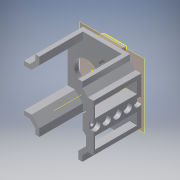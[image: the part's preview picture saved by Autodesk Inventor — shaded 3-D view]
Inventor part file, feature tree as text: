
AUTODESK INVENTOR PART (.ipt)
format: ipt  version: 2019 (Build 230136000, 136)  size: 473,088 bytes
history: native  units: mm
features: reference x25, other x11, sketch x10, extrude x9, projected_geometry x6, plane x5, chamfer x2, hole x2, pattern_circular x1, pattern_linear x1, fillet x1
ambient origin geometry x8: Origin, YZ Plane, XZ Plane, XY Plane, X Axis, Y Axis, Z Axis, Center Point
bodies: Solid1 (feature_tree)
feature tree (73):
  plane  "Work Plane1"
  extrude  "Extrusion1"  Depth=0.1mm
  chamfer  "Chamfer1"  Distance=3.0mm
  sketch  "Sketch2"  dims[d3=0.1mm]
  plane  "Work Plane2"
  extrude  "Extrusion2"  Depth=3.001102mm
  other  "Work Axis1"
  pattern_circular  "Circular Pattern1"  Count=4 Angle=360.0deg
  extrude  "Extrusion3"  Depth=1.0mm TaperAngle=0.0deg
  sketch  "Sketch4"  dims[d5=0.1mm]
  plane  "Work Plane3"
  extrude  "Extrusion4"  Depth=49.7mm
  extrude  "Extrusion5"  Depth=49.7mm
  pattern_linear  "Rectangular Pattern1"  Spacing1=2.8mm  [1 undecoded]
  sketch  "Sketch7"  dims[d6=3.0mm]
  plane  "Work Plane4"
  extrude  "Extrusion7"  Depth=10.0mm TaperAngle=0.0deg
  hole  "Hole1"  [1 undecoded]
  extrude  "Extrusion8"  Depth=19.0mm
  extrude  "Extrusion9"  TaperAngle=0.0deg  [1 undecoded]
  hole  "Hole2"  [1 undecoded]
  chamfer  "Chamfer2"  Distance=2.0mm
  fillet  "Fillet1"  Radius=3.0mm
  sketch  "Sketch14"  dims[d19=6.0mm d20=1.0mm d21=0.0mm]
  sketch  "Sketch15"  dims[d22=3.0mm d23=0.0mm d24=2.0mm d25=2.8mm d26=2.8mm d27=10.0mm d28=0.0mm d29=40.0mm d31=7.5mm d35=19.0mm d36=0.0mm d37=12.0mm d38=0.0mm d39=2.5mm d40=6.0mm d41=6.0mm d42=22.0mm d43=90.0deg d44=8.0mm d45=20.594885mm d46=2.0mm d47=3.0mm d48=0.0mm d50=3.0mm d51=0.0mm d56=2.8mm d57=6.0mm d58=6.0mm d59=3.0mm d60=90.0deg d61=8.0mm d62=20.594885mm d68=2.0mm d69=2.0mm d70=45.0deg d71=3.0mm d72=0.0mm d73=4.0mm d74=16.45mm d75=16.45mm d76=12.53mm d77=23.0mm d78=11.5mm d79=11.5mm d80=11.5mm d81=18.0mm d82=2.5mm d83=7.719987mm d84=10.0mm d85=0.0mm d86=49.7mm d87=24.85mm d88=0.0mm]
  plane  "Work Plane5"
  extrude  "Extrusion12"  Depth=3.0mm TaperAngle=0.0deg
  sketch  "Sketch1"  dims[d1=0.1mm d2=0.1mm]
  reference  "Reference2"
  reference  "Reference3"
  reference  "Reference4"
  reference  "Reference5"
  reference  "Reference6"
  reference  "Reference7"
  projected_geometry  "Projected Loop1"
  sketch  "Sketch3"  dims[d4=0.1mm]
  reference  "Reference8"
  projected_geometry  "Projected Loop2"
  projected_geometry  "Projected Loop3"
  reference  "Reference9"
  reference  "Reference10"
  reference  "Reference11"
  reference  "Reference13"
  reference  "Reference14"
  reference  "Reference15"
  reference  "Reference16"
  projected_geometry  "Projected Loop5"
  reference  "Reference17"
  reference  "Reference18"
  reference  "Reference19"
  sketch  "Sketch9"  dims[d7=3.0mm d8=3.0mm d9=0.0mm]
  reference  "Reference20"
  sketch  "Sketch10"  dims[d10=3.9mm d11=2.0mm d12=45.0deg d13=3.001102mm]
  reference  "Reference22"
  sketch  "Sketch12"  dims[d14=6.0mm d15=0.0mm d16=40.0mm d17=360.0deg]
  reference  "Reference23"
  projected_geometry  "Projected Loop8"
  reference  "Reference28"
  reference  "Reference29"
  reference  "Reference30"
  projected_geometry  "Projected Loop9"
  reference  "Reference32"
  reference  "Reference33"
  other  "<userpath>\Downloads\cellSTORM\Assembly_Cube_Z_Focus_MGN_NEMA_v3.iam"
  other  "Assembly_Cube_Z_Focus_MGN_NEMA_v3.iam"
  other  "Assembly_Cube_empty_IM_v3:1"
  other  "10_Cube_1x1_IM:2"
  other  "10_Cube_1x1_IM:1"
  other  "00_NEMA11:1"
  other  "DIN 912 - replaced by DIN EN ISO 4762 M3 x 30:1"
  other  "00_MGN12 LINEAR GUIDE RAIL, CONFIGURABLE:1"
  other  "Assembly_Cube_empty_IM_v3:2"
  other  "30_Cube_Z_Focus_MGN_NEMA_rail:1"
note: 4 required parameter values undecoded (feature->parameter linkage not recoverable at this tier; creation-order binding heuristic only, values carry confidence <= 0.55)
